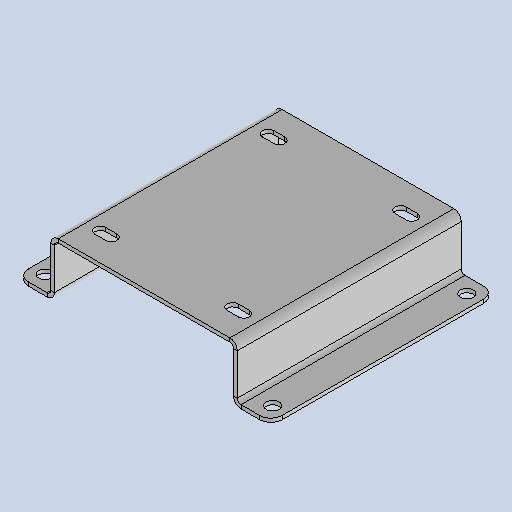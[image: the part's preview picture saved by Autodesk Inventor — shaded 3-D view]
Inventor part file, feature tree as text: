
AUTODESK INVENTOR PART (.ipt)
format: ipt  version: 2025.3 (Build 293356030, 356C)  size: 249,856 bytes
history: native  units: mm
features: sheet_metal_op x7, other x6, sketch x5, mirror x1, chamfer x1
ambient origin geometry x8: Origin, YZ Plane, XZ Plane, XY Plane, X Axis, Y Axis, Z Axis, Center Point
bodies: Solid1 (feature_tree)
feature tree (20):
  sheet_metal_op  "Face1"
  sheet_metal_op  "Flange2"
  sheet_metal_op  "Flange3"
  mirror  "Mirror1"
  chamfer  "Corner Round1"
  sketch  "Sketch1"  dims[d0=100.0mm]
  other  "Plate1"
  sketch  "Sketch5"  dims[d1=120.0mm]
  other  "Plate3"
  sheet_metal_op  "Bend2"
  sheet_metal_op  "Corner2"
  sketch  "Sketch6"  dims[d2=2.0mm]
  other  "Plate4"
  sheet_metal_op  "Bend3"
  sheet_metal_op  "Corner3"
  sketch  "Sketch7"  dims[d22=2.0mm]
  sketch  "Sketch8"  dims[d23=1.0mm d24=4.0mm d25=2.0mm d26=30.0mm d27=90.0deg d28=2.0mm d29=8.0mm d30=2.0mm d31=2.0mm d32=2.0mm d33=1.0mm d34=4.0mm d35=2.0mm d36=20.0mm d37=90.0deg d38=2.0mm d39=8.0mm d40=2.0mm d41=2.0mm d42=6.0mm d43=6.0mm d50=71.0mm d51=90.0mm d52=2.0mm d53=0.0mm d54=7.0mm d55=8.0mm d56=7.0mm d57=2.0mm d58=0.0mm d59=6.0mm]
  other  "Cut1"
  other  "Cut2"
  other  "Definition1"
